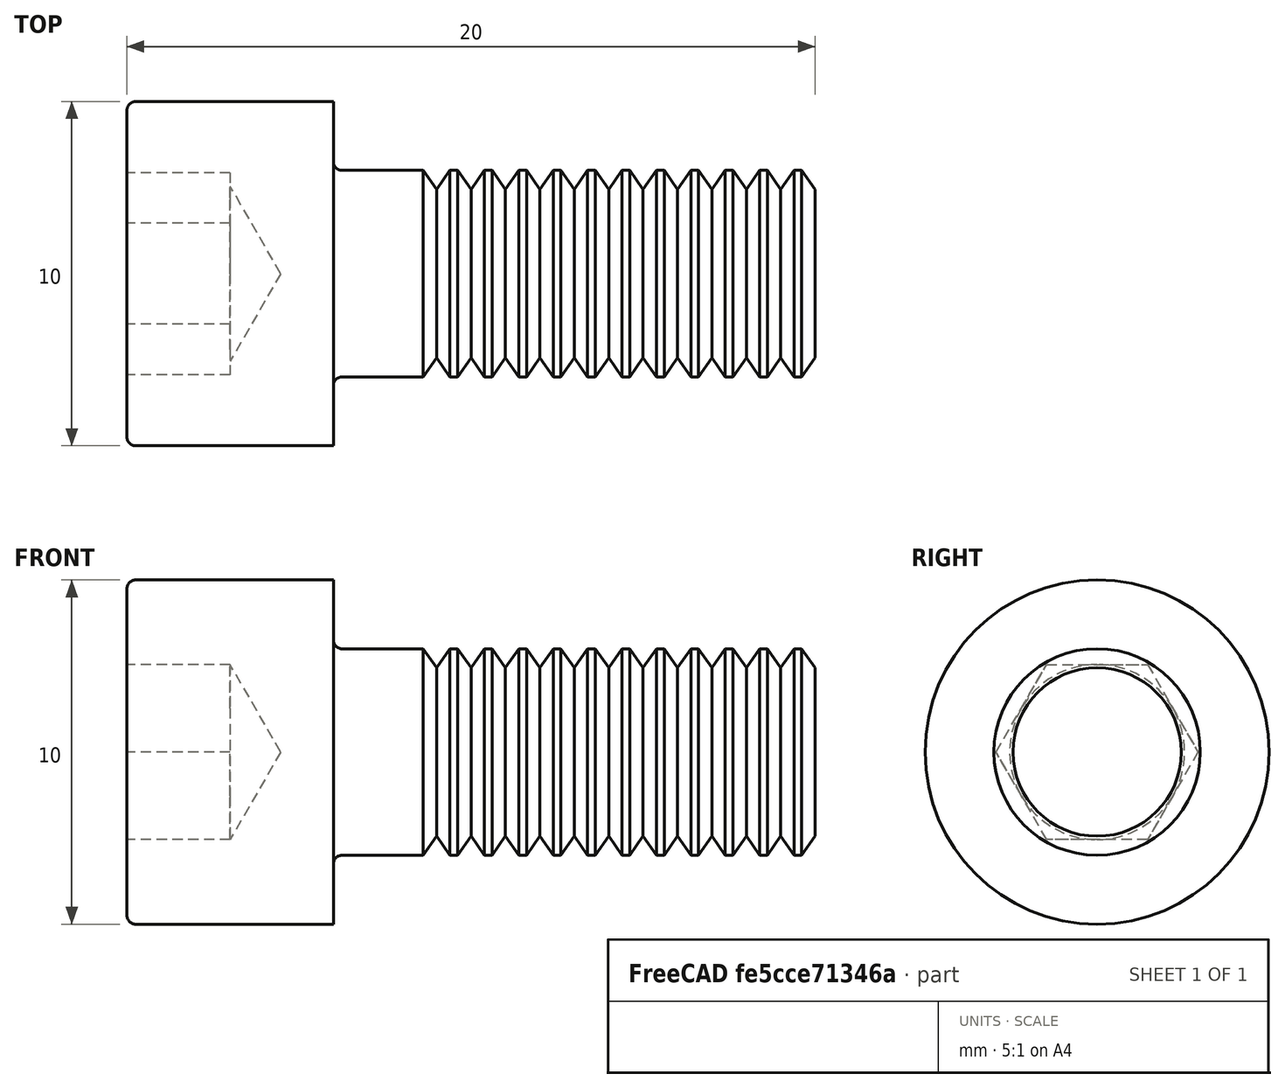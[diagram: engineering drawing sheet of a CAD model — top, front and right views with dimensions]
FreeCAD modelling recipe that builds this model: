
FCSTD DOCUMENT  (FreeCAD 0.21R33771 (Git))
Label: m6x14_screw
License: All rights reserved
LicenseURL: http://en.wikipedia.org/wiki/All_rights_reserved
objects: Part::Feature×1, Sketcher::SketchObject×1, PartDesign::FeatureBase×1, PartDesign::Pocket×1, PartDesign::Body×1
note: 6 computed .brp shape members not serialized (recipe doc carries the construction recipe); baked Part::Feature solids carry a one-line shape summary decoded from their .brp

FEATURE [Part::Feature] Part__Feature004  label="m6"
  shape: bbox 26 x 10.82 x 10.82 mm, 129 faces (baked)
FEATURE [Sketcher::SketchObject] Sketch
  FullyConstrained = false
  MapMode = 5
  Placement = pos=(15.8921,0,0) rot=(0.57735,0.57735,0.57735;2.0944rad)
  Support = -> [Part__Feature004]
  sketch-geometry (1):
    g0: Circle CenterX=0 CenterY=0 CenterZ=0 NormalX=0 NormalY=0 NormalZ=1 AngleXU=0 Radius=9.23049
  constraints (1):
    c: Coincident(g0,g-1)
FEATURE [PartDesign::FeatureBase] BaseFeature
  BaseFeature = -> Part__Feature004
FEATURE [PartDesign::Pocket] Pocket
  BaseFeature = -> BaseFeature
  Direction = (-1,0,0)
  Length = 6
  Length2 = 5
  Profile = -> Sketch
  ReferenceAxis = -> Sketch [N_Axis]
  Refine = true
  Type = 0
FEATURE [PartDesign::Body] Body
  BaseFeature = -> Part__Feature004
  Group = -> [BaseFeature,Sketch,Pocket]
  Origin = -> Origin
  Tip = -> Pocket
